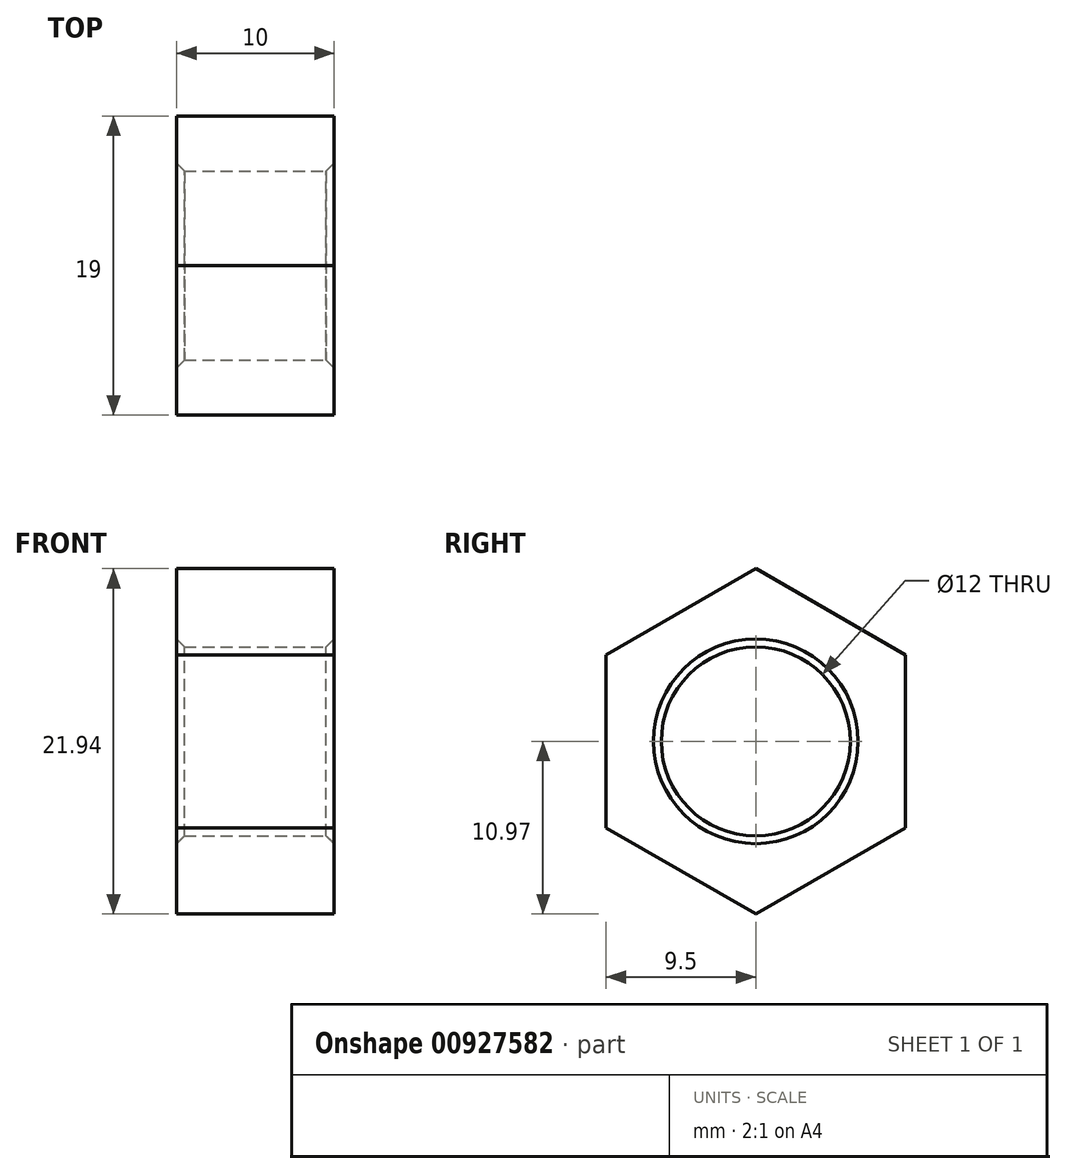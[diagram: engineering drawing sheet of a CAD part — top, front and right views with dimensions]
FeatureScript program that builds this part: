
annotation { "Feature Type Name" : "Feature", "Feature Type Description" : "" }
export const myFeature = defineFeature(function(context is Context, id is Id, definition is map)
    precondition{}
    {
        {
            var Q0;
            Q0=qCreatedBy(makeId("Right.planeOp"),FACE);
            var sketch = newSketch(context, id + "F0", { "sketchPlane" : qUnion([Q0])});
            skLineSegment(sketch, "E0", {"start": v(0, 33.7) * mm, "end": v(0, -33.7) * mm, "construction": true});
            skLineSegment(sketch, "E1", {"start": v(-43.42, 0) * mm, "end": v(52.92, 0) * mm, "construction": true});
            skCircle(sketch, "E2.cCircle", {"center": v(0, 0) * mm, "radius": 9.5 * mm, "construction": true});
            skPoint(sketch, "E2.cCircle.perimeterSnap0", {"position": v(4.75, 0) * mm});
            skLineSegment(sketch, "E2.0", {"start": v(9.5, -5.48) * mm, "end": v(0, -10.97) * mm});
            skLineSegment(sketch, "E2.1", {"start": v(0, -10.97) * mm, "end": v(-9.5, -5.48) * mm});
            skLineSegment(sketch, "E2.2", {"start": v(-9.5, -5.48) * mm, "end": v(-9.5, 5.48) * mm});
            skLineSegment(sketch, "E2.3", {"start": v(-9.5, 5.48) * mm, "end": v(0, 10.97) * mm});
            skLineSegment(sketch, "E2.4", {"start": v(0, 10.97) * mm, "end": v(9.5, 5.48) * mm});
            skLineSegment(sketch, "E2.5", {"start": v(9.5, 5.48) * mm, "end": v(9.5, -5.48) * mm});
            skPoint(sketch, "E2.0.midPoint", {"position": v(4.75, -8.23) * mm});
            skPoint(sketch, "E2.0.midPoint.positionSnap0", {"position": v(4.75, 0) * mm});
            skSolve(sketch);
        }
        {
            var Q0;
            Q0 = qSketchRegion(id + "F0", true);
            extrude(context, id + "F1", {"entities" : qUnion([Q0]), "oppositeDirection" : true, "depth" : 10 * mm, "offsetDistance" : 25 * mm});
        }
        {
            var Q0;
            Q0=makeQuery(id+"F1.opExtrude","CAP_FACE",FACE,{"disambiguationData":[OSD([sQuery(id+"F0.wireOp",EDGE,"E2.0"),sQuery(id+"F0.wireOp",EDGE,"E2.1"),sQuery(id+"F0.wireOp",EDGE,"E2.2"),sQuery(id+"F0.wireOp",EDGE,"E2.3"),sQuery(id+"F0.wireOp",EDGE,"E2.4"),sQuery(id+"F0.wireOp",EDGE,"E2.5")])],"isStart":true});
            var sketch = newSketch(context, id + "F2", { "sketchPlane" : qUnion([Q0])});
            skCircle(sketch, "E3", {"center": v(0, 0) * mm, "radius": 6 * mm});
            skSolve(sketch);
        }
        {
            var Q0;
            Q0 = qSketchRegion(id + "F2", true);
            extrude(context, id + "F3", {"entities" : qUnion([Q0]), "operationType" : NewBodyOperationType.REMOVE, "endBound" : BoundingType.THROUGH_ALL, "oppositeDirection" : true, "depth" : 25 * mm, "offsetDistance" : 25 * mm});
        }
        {
            var Q0;
            Q0=makeQuery(id+"F3.boolean.opBoolean","COPY",FACE,{"derivedFrom":makeQuery(id+"F3.opExtrude","SWEPT_FACE",FACE,{"disambiguationData":[OSD([sQuery(id+"F2.wireOp",EDGE,"E3")])]})});
            chamfer(context, id + "F4", {"entities" : qUnion([Q0]), "width" : 0.5 * mm, "tangentPropagation" : true});
        }
    });
